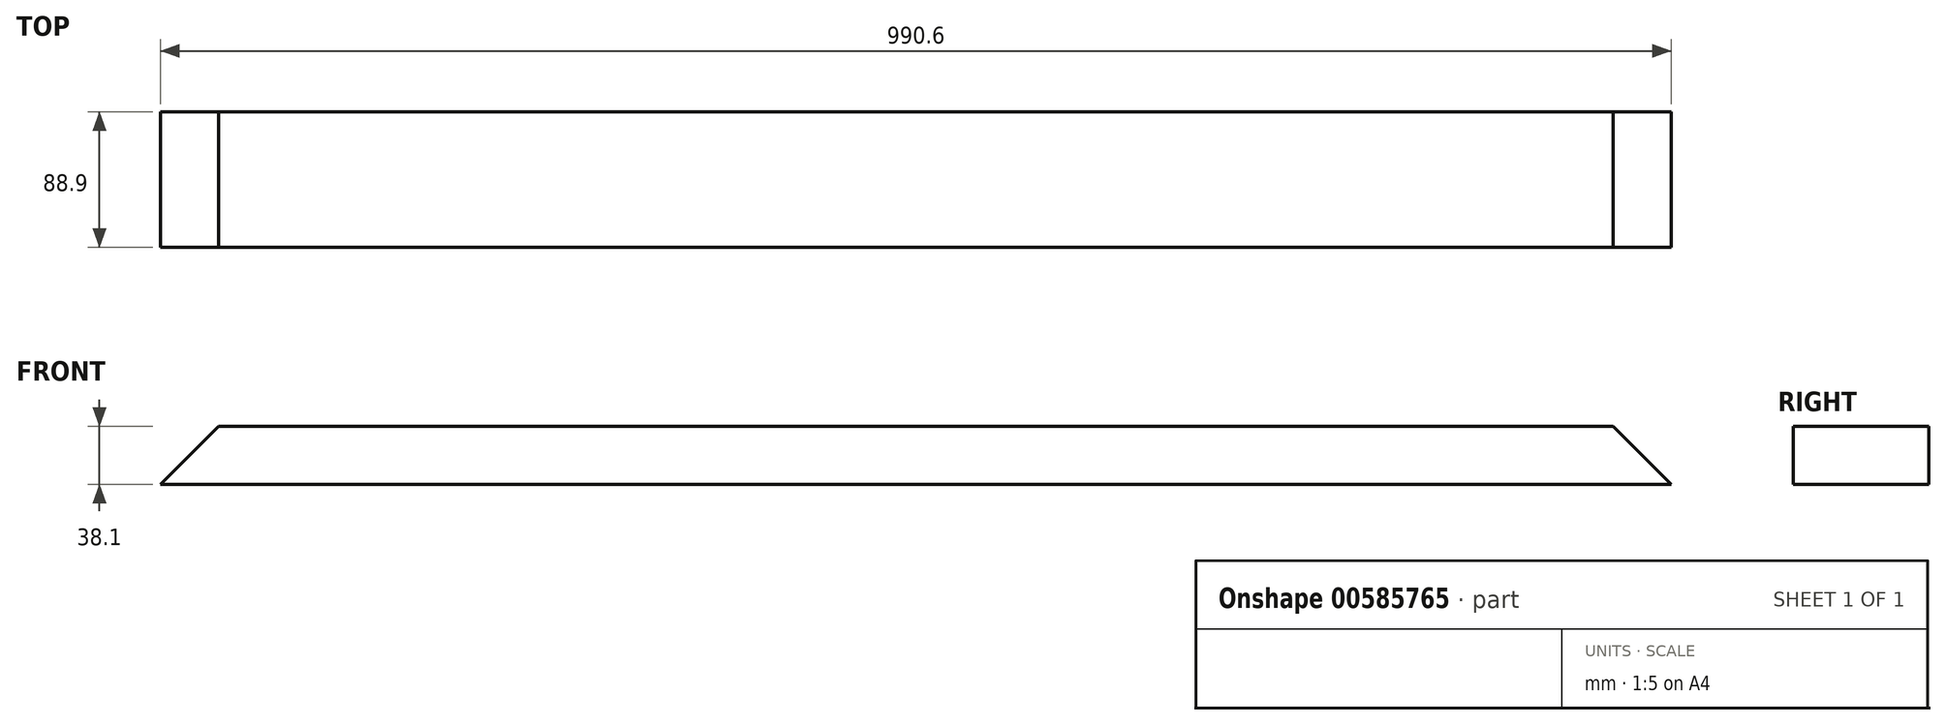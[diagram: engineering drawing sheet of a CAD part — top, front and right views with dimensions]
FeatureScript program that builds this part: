
annotation { "Feature Type Name" : "Feature", "Feature Type Description" : "" }
export const myFeature = defineFeature(function(context is Context, id is Id, definition is map)
    precondition{}
    {
        {
            var Q0;
            Q0=qCreatedBy(makeId("Front.planeOp"),FACE);
            var sketch = newSketch(context, id + "F0", { "sketchPlane" : qUnion([Q0])});
            skLineSegment(sketch, "E0", {"start": v(0, 0) * mm, "end": v(-990.6, 0) * mm});
            skLineSegment(sketch, "E1", {"start": v(-990.6, 0) * mm, "end": v(-952.5, 38.1) * mm});
            skLineSegment(sketch, "E2", {"start": v(-952.5, 38.1) * mm, "end": v(-38.1, 38.1) * mm});
            skLineSegment(sketch, "E3", {"start": v(-38.1, 38.1) * mm, "end": v(0, 0) * mm});
            skSolve(sketch);
        }
        {
            var Q0;
            Q0=makeQuery(id+"F0.imprint","IMPRINT",FACE,{"disambiguationData":[TD([[makeQuery(id+"F0.imprint","IMPRINT",EDGE,{"derivedFrom":sQuery(id+"F0.wireOp",EDGE,"E0")}),-1.0]])]});
            extrude(context, id + "F1", {"entities" : qUnion([Q0]), "depth" : 88.9 * mm, "offsetDistance" : 25.4 * mm});
        }
    });
